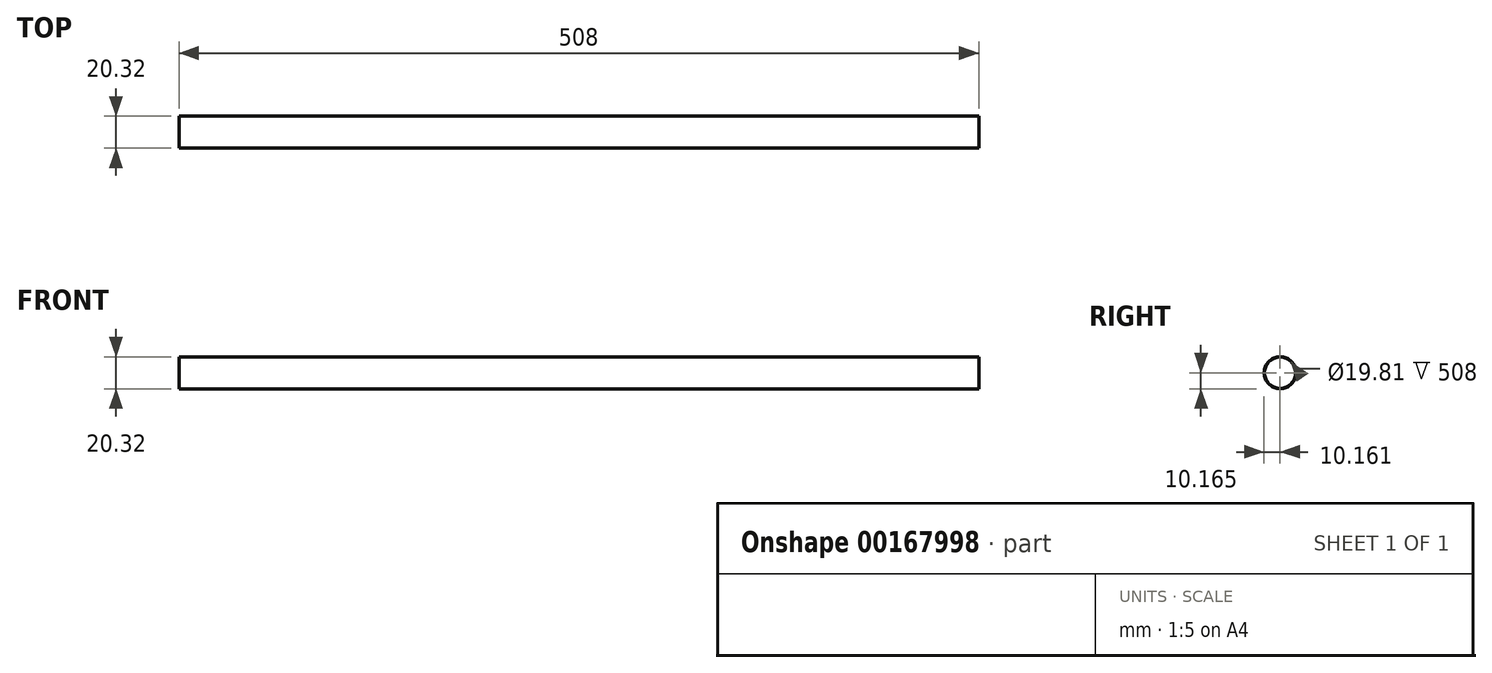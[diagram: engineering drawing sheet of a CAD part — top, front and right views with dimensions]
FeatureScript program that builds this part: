
annotation { "Feature Type Name" : "Feature", "Feature Type Description" : "" }
export const myFeature = defineFeature(function(context is Context, id is Id, definition is map)
    precondition{}
    {
        {
            var Q0;
            Q0=qCreatedBy(makeId("Right.planeOp"),FACE);
            var sketch = newSketch(context, id + "F0", { "sketchPlane" : qUnion([Q0])});
            skCircle(sketch, "E0", {"center": v(-14.4, 14.23) * mm, "radius": 9.9 * mm});
            skCircle(sketch, "E1", {"center": v(-14.4, 14.23) * mm, "radius": 10.16 * mm});
            skSolve(sketch);
        }
        {
            var Q0;
            Q0=makeQuery(id+"F0.imprint","IMPRINT",FACE,{"disambiguationData":[TD([[makeQuery(id+"F0.imprint","IMPRINT",EDGE,{"derivedFrom":sQuery(id+"F0.wireOp",EDGE,"E0")}),-1.0]])]});
            extrude(context, id + "F1", {"entities" : qUnion([Q0]), "depth" : 508 * mm});
        }
    });
